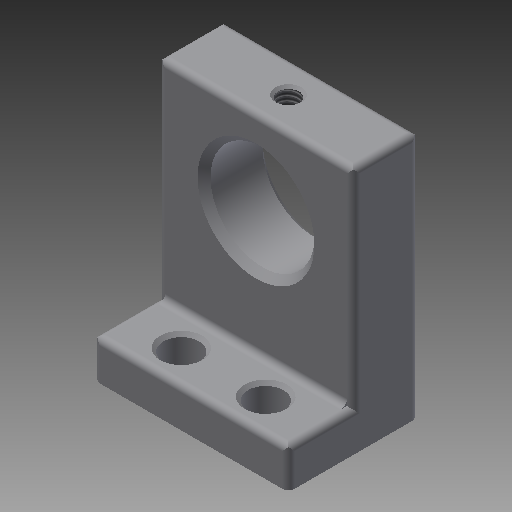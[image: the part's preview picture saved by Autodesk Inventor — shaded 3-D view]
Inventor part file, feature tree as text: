
AUTODESK INVENTOR PART (.ipt)
format: ipt  version: 2019 (Build 230136000, 136)  size: 231,936 bytes
history: native  units: mm
features: sketch x11, extrude x7, other x7, revolve x2, hole x2, thread x1
ambient origin geometry x8: Origin, YZ Plane, XZ Plane, XY Plane, X Axis, Y Axis, Z Axis, Center Point
bodies: Solid1 (feature_tree)
feature tree (30):
  sketch  "Sketch_9"
  sketch  "Sketch_10"
  extrude  "Extrusion1"  Depth=38.0mm TaperAngle=0.0deg
  extrude  "Extrusion2"  TaperAngle=360.0deg  [1 undecoded]
  extrude  "Extrusion3"  Depth=4.621mm TaperAngle=0.0deg
  revolve  "Revolution1"  [1 undecoded]
  revolve  "Revolution2"  [1 undecoded]
  thread  "Thread1"  [1 undecoded]
  hole  "Hole1"  [1 undecoded]
  hole  "Hole2"  [1 undecoded]
  extrude  "Extrusion4"  [1 undecoded]
  extrude  "Extrusion5"  [1 undecoded]
  extrude  "Extrusion6"  [1 undecoded]
  extrude  "Extrusion7"  [1 undecoded]
  other  "b_s_XY"
  other  "b_s_YZ"
  other  "b_s_ZX"
  other  "b_s_X"
  other  "b_s_Y"
  other  "b_s_Z"
  other  "b_s_Center"
  sketch  "Sketch_5"  dims[d7=360.0deg d8=4.621mm d9=0.0mm]
  sketch  "Sketch_7"  dims[d26=0.8mm d27=0.0mm d28=30.0mm d29=0.0mm d30=28.0mm d31=0.0mm]
  sketch  "Sketch_1"  dims[d0=20.0mm d1=0.0mm d2=38.0mm d3=0.0mm]
  sketch  "Sketch6"  dims[d10=5.5mm d11=6.0mm d12=6.5mm d13=2.0mm d14=90.0deg d15=6.0mm d16=0.0mm]
  sketch  "Sketch7"  dims[d32=0.0mm]
  sketch  "Sketch_4"  dims[d4=10.0mm d5=0.0mm d6=360.0deg]
  sketch  "Sketch_8"
  sketch  "Sketch_6"  dims[d17=5.5mm d18=6.0mm d19=6.5mm d20=2.0mm d21=90.0deg d22=6.0mm d23=0.0mm d24=38.0mm d25=0.0mm]
  sketch  "Sketch_11"
note: 10 required parameter values undecoded (feature->parameter linkage not recoverable at this tier; creation-order binding heuristic only, values carry confidence <= 0.55)